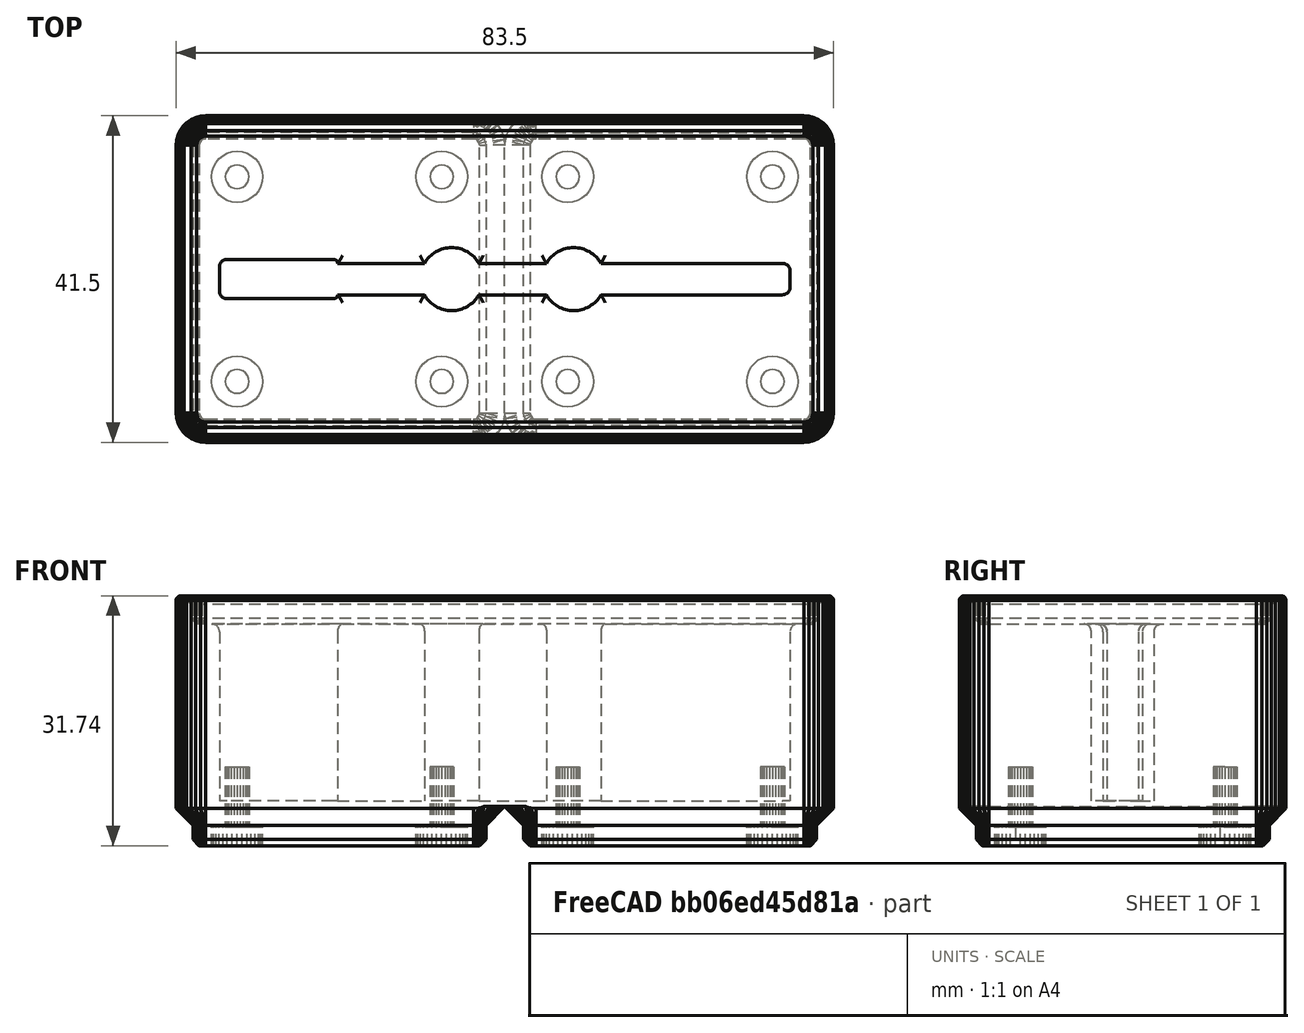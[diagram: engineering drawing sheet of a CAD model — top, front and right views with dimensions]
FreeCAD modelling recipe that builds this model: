
FCSTD DOCUMENT  (FreeCAD 0.21R33694 (Git))
Label: gridfinity_1x2_rakel
License: All rights reserved
LicenseURL: http://en.wikipedia.org/wiki/All_rights_reserved
objects: Part::Feature×2, Sketcher::SketchObject×2, PartDesign::Fillet×2, PartDesign::FeatureBase×1, Mesh::Feature×1, Part::Refine×1, PartDesign::Plane×1, PartDesign::Pocket×1, PartDesign::Body×1
note: 14 computed .brp shape members not serialized (recipe doc carries the construction recipe); baked Part::Feature solids carry a one-line shape summary decoded from their .brp

FEATURE [Part::Feature] _x2_Block_1_25in001001_solid  label="_x2_Block_1_25in001001 (Solid)"
  shape: bbox 83.5 x 41.5 x 31.74 mm, 1626 faces (baked)
FEATURE [PartDesign::FeatureBase] BaseFeature
  BaseFeature = -> _x2_Block_1_25in001001_solid
FEATURE [Mesh::Feature] _x2_Block_1_25in  label="1x2 Block 1.25in"
FEATURE [Part::Feature] _x2_Block_1_25in001
  shape: bbox 83.5 x 41.5 x 31.74 mm, 4368 faces, 0 solids (baked)
FEATURE [Part::Refine] _x2_Block_1_25in001001
  Source = -> _x2_Block_1_25in001
FEATURE [PartDesign::Plane] DatumPlane
  AttachmentOffset = pos=(0,0,28.2) rot=(0,0,1;0rad)
  Length = 125.79
  MapMode = 5
  Placement = pos=(0,0,28.2) rot=(0,0,1;0rad)
  ResizeMode = 0
  Support = -> [XY_Plane]
  Width = 83.79
FEATURE [Sketcher::SketchObject] Sketch001  label="Sketch_backup"
  FullyConstrained = true
  MapMode = 5
  Placement = pos=(0,0,28.2) rot=(0,0,1;0rad)
  Support = -> [DatumPlane]
  expr: Constraints[16] = 42 / 2 - 4 / 2
  expr: Constraints[17] = (42 * 2 - 72) / 2
  sketch-geometry (6):
    g0: LineSegment StartX=6 StartY=23 StartZ=0 EndX=78 EndY=23 EndZ=0
    g1: LineSegment StartX=78 StartY=23 StartZ=0 EndX=78 EndY=19 EndZ=0
    g2: LineSegment StartX=78 StartY=19 StartZ=0 EndX=6 EndY=19 EndZ=0
    g3: LineSegment StartX=6 StartY=19 StartZ=0 EndX=6 EndY=23 EndZ=0
    g4: Circle CenterX=35.25 CenterY=21 CenterZ=0 NormalX=0 NormalY=0 NormalZ=1 AngleXU=0 Radius=4
    g5: Circle CenterX=50.75 CenterY=21 CenterZ=0 NormalX=0 NormalY=0 NormalZ=1 AngleXU=0 Radius=4
  constraints (18):
    c: Coincident(g0,g1)
    c: Coincident(g1,g2)
    c: Coincident(g2,g3)
    c: Coincident(g3,g0)
    c: Horizontal(g0)
    c: Horizontal(g2)
    c: Vertical(g1)
    c: Vertical(g3)
    c: DistanceX(g0,g0) = 72
    c: DistanceY(g1,g1) = 4
    c: Equal(g4,g5)
    c: Diameter(g4) = 8
    c: DistanceX(g4,g5) = 15.5
    c: Distance(g4,g3) = 29.25
    c: Horizontal(g5,g4)
    c: DistanceY(g1,g5) = 2
    c: DistanceY(g-1,g2) = 19
    c: DistanceX(g-1,g2) = 6
FEATURE [Sketcher::SketchObject] Sketch002  label="Sketch"
  FullyConstrained = false
  MapMode = 5
  Placement = pos=(0,0,28.2) rot=(0,0,1;0rad)
  Support = -> [DatumPlane]
  expr: Constraints[17] = (42 * 2 - 72.5) / 2
  expr: Constraints[19] = 42 / 2 - 5 / 2
  sketch-geometry (16):
    g0: LineSegment StartX=20.75 StartY=23 StartZ=0 EndX=31.7859 EndY=23 EndZ=0
    g1: LineSegment StartX=78.25 StartY=23 StartZ=0 EndX=78.25 EndY=19 EndZ=0
    g2: LineSegment StartX=78.25 StartY=19 StartZ=0 EndX=54.2141 EndY=19 EndZ=0
    g3: ArcOfCircle CenterX=35.25 CenterY=21 CenterZ=0 NormalX=0 NormalY=0 NormalZ=1 AngleXU=0 Radius=4 StartAngle=3.66519 EndAngle=5.75959
    g4: ArcOfCircle CenterX=50.75 CenterY=21 CenterZ=0 NormalX=0 NormalY=0 NormalZ=1 AngleXU=0 Radius=4 StartAngle=3.66519 EndAngle=5.75959
    g5: LineSegment StartX=5.75 StartY=18.5 StartZ=0 EndX=20.25 EndY=18.5 EndZ=0
    g6: LineSegment StartX=20.25 StartY=23.5 StartZ=0 EndX=5.75 EndY=23.5 EndZ=0
    g7: LineSegment StartX=5.75 StartY=23.5 StartZ=0 EndX=5.75 EndY=18.5 EndZ=0
    g8: LineSegment StartX=38.7141 StartY=23 StartZ=0 EndX=47.2859 EndY=23 EndZ=0
    g9: LineSegment StartX=31.7859 StartY=19 StartZ=0 EndX=20.75 EndY=19 EndZ=0
    g10: ArcOfCircle CenterX=35.25 CenterY=21 CenterZ=0 NormalX=0 NormalY=0 NormalZ=1 AngleXU=0 Radius=4 StartAngle=0.523599 EndAngle=2.61799
    g11: LineSegment StartX=54.2141 StartY=23 StartZ=0 EndX=78.25 EndY=23 EndZ=0
    g12: LineSegment StartX=47.2859 StartY=19 StartZ=0 EndX=38.7141 EndY=19 EndZ=0
    g13: ArcOfCircle CenterX=50.75 CenterY=21 CenterZ=0 NormalX=0 NormalY=0 NormalZ=1 AngleXU=0 Radius=4 StartAngle=0.523599 EndAngle=2.61799
    g14: ArcOfCircle CenterX=20.25 CenterY=23 CenterZ=0 NormalX=0 NormalY=0 NormalZ=1 AngleXU=0 Radius=0.5 StartAngle=0 EndAngle=1.5708
    g15: ArcOfCircle CenterX=20.25 CenterY=19 CenterZ=0 NormalX=0 NormalY=0 NormalZ=1 AngleXU=0 Radius=0.5 StartAngle=4.71239 EndAngle=6.28319
  constraints (36):
    c: Coincident(g11,g1)
    c: Coincident(g1,g2)
    c: Horizontal(g0)
    c: Horizontal(g2)
    c: Vertical(g1)
    c: DistanceY(g1,g1) = 4
    c: Equal(g3,g4)
    c: Diameter(g3) = 8
    c: DistanceX(g3,g4) = 15.5
    c: Horizontal(g4,g3)
    c: DistanceY(g1,g4) = 2
    c: Coincident(g6,g7)
    c: Coincident(g7,g5)
    c: Horizontal(g5)
    c: Horizontal(g6)
    c: Vertical(g7)
    c: DistanceX(g5,g5) = 14.5
    c: DistanceX(g-1,g5) = 5.75
    c: DistanceY(g5,g6) = 5
    c: DistanceY(g-1,g5) = 18.5
    c: Coincident(g10,g0)
    c: Coincident(g9,g3)
    c: Equal(g3,g10)
    c: Coincident(g3,g12)
    c: Coincident(g10,g8)
    c: Coincident(g3,g10)
    c: Coincident(g8,g13)
    c: Coincident(g12,g4)
    c: Equal(g4,g13)
    c: Coincident(g4,g2)
    c: Coincident(g13,g11)
    c: Coincident(g4,g13)
    c: Coincident(g14,g6)
    c: Coincident(g0,g14)
    c: Coincident(g15,g5)
    c: Coincident(g9,g15)
FEATURE [PartDesign::Pocket] Pocket
  BaseFeature = -> BaseFeature
  Direction = (0,0,-1)
  Length = 22.5
  Length2 = 5
  Profile = -> Sketch002
  ReferenceAxis = -> Sketch002 [N_Axis]
  Type = 0
FEATURE [PartDesign::Fillet] Fillet
  Base = -> Pocket [Edge3051,Edge3053,Edge3070,Edge3068]
  BaseFeature = -> Pocket
  Radius = 1
  SupportTransform = false
  UseAllEdges = false
FEATURE [PartDesign::Fillet] Fillet001
  Base = -> Fillet [Edge1,Edge5,Edge7,Edge9,Edge13,Edge11,Edge8,Edge12,Edge14,Edge16,Edge18,Edge20,Edge17,Edge4]
  BaseFeature = -> Fillet
  Radius = 1
  SupportTransform = false
  UseAllEdges = false
FEATURE [PartDesign::Body] Body
  BaseFeature = -> _x2_Block_1_25in001001_solid
  Group = -> [BaseFeature,DatumPlane,Sketch002,Pocket,Fillet,Fillet001]
  Origin = -> Origin
  Tip = -> Fillet001
